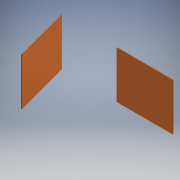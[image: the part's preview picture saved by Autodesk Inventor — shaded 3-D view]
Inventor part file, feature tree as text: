
AUTODESK INVENTOR PART (.ipt)
format: ipt  version: 2016 (Build 200138000, 138)  size: 163,840 bytes
history: native  units: mm
features: extrude x3, sketch x3, projected_geometry x1
ambient origin geometry x8: Origin, YZ Plane, XZ Plane, XY Plane, X Axis, Y Axis, Z Axis, Center Point
bodies: Solid1 (feature_tree)
feature tree (7):
  extrude  "Extrusion1"  Depth=50.0mm
  extrude  "Extrusión10"  Depth=6.0mm
  extrude  "Extrusión11"  TaperAngle=0.0deg  [1 undecoded]
  sketch  "Sketch1"  dims[d2=41.0mm d3=50.0mm]
  sketch  "Boceto10"  dims[d4=100.0mm d5=6.0mm]
  sketch  "Boceto11"  dims[d6=6.0mm d8=0.0mm d49=721.666667mm d50=721.666667mm d52=10.0mm d53=721.666667mm d54=820.0mm d55=0.0mm d56=41.0mm d57=50.0mm d58=100.0mm d59=6.0mm d60=6.0mm d61=820.0mm d62=0.0mm]
  projected_geometry  "Contorno proyectado8"
note: 1 required parameter value undecoded (feature->parameter linkage not recoverable at this tier; creation-order binding heuristic only, values carry confidence <= 0.55)
